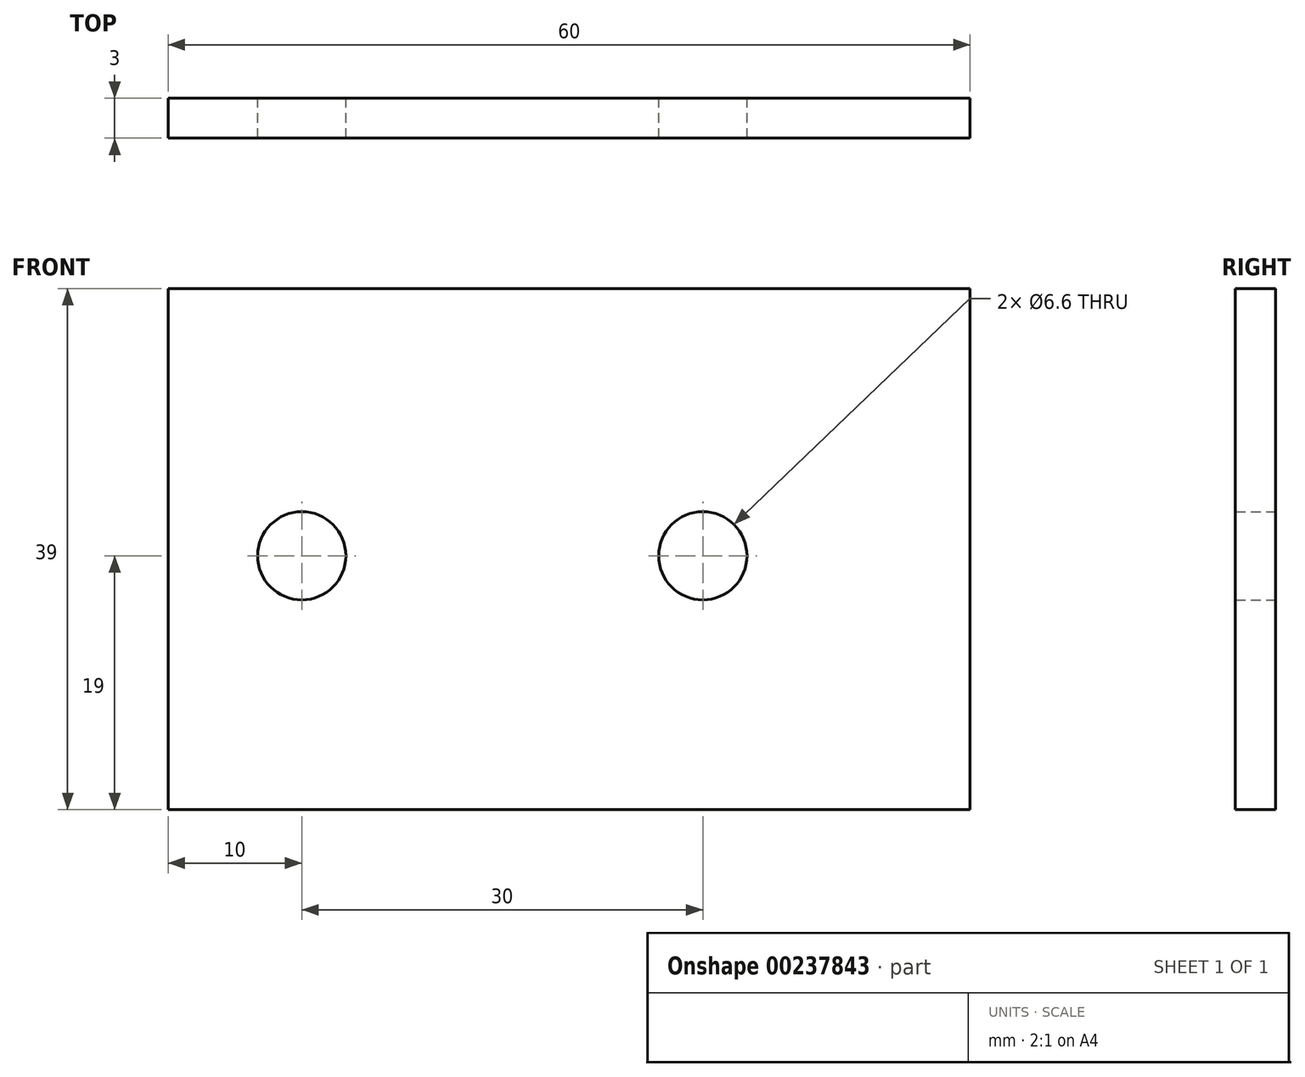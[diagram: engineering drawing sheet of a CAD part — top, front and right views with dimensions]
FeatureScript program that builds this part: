
annotation { "Feature Type Name" : "Feature", "Feature Type Description" : "" }
export const myFeature = defineFeature(function(context is Context, id is Id, definition is map)
    precondition{}
    {
        {
            var Q0;
            Q0=qCreatedBy(makeId("Front.planeOp"),FACE);
            var sketch = newSketch(context, id + "F0", { "sketchPlane" : qUnion([Q0])});
            skLineSegment(sketch, "E0.bottom", {"start": v(0, 0) * mm, "end": v(60, 0) * mm});
            skLineSegment(sketch, "E0.top", {"start": v(0, -39) * mm, "end": v(60, -39) * mm});
            skLineSegment(sketch, "E0.left", {"start": v(0, 0) * mm, "end": v(0, -39) * mm});
            skLineSegment(sketch, "E0.right", {"start": v(60, 0) * mm, "end": v(60, -39) * mm});
            skCircle(sketch, "E1", {"center": v(10, -20) * mm, "radius": 3.3 * mm});
            skCircle(sketch, "E2", {"center": v(40, -20) * mm, "radius": 3.3 * mm});
            skSolve(sketch);
        }
        {
            var Q0;
            Q0 = qSketchRegion(id + "F0", true);
            extrude(context, id + "F1", {"entities" : qUnion([Q0]), "depth" : 3 * mm});
        }
    });
